# Revit family: E108.01.05_D9
name_source: partatom
category: Plumbing Fixtures
units: mm (PartAtom-declared; Revit-internal decimal feet)

## family parameters
Always vertical = Yes
Cut with Voids When Loaded = No
OmniClass Number = 23.45.05.14
OmniClass Title = Plumbing Fixtures - Sanitary Washing Units
Part Type = Normal
Room Calculation Point = No
Round Connector Dimension = Use Diameter
Shared = No
Work Plane-Based = No

## types (1)
- Standard
    Acabado = Cromo
    CW Connection = No
    Catalog web link = https://fvandina.com
    Certificación = INEN
    Conexión hidráulica = ½ x 14 NPT
    Cota alto = 150 mm
    Cota ancho = 120 mm
    Cota largo = 68 mm
    Default Elevation = 0 mm  [stored 0 ft]
    Description = Juego Mezclador Monocomando para Ducha COTY
    Dirección fabricante = KM 25, VÍA SANGOLQUÍ AMAGUAÑA - PICHINCHA - ECUADOR
    Garantía = GARANTÍA TOTAL FV - DETALLES EN PÁGINA WEB
    HW Connection = No
    Instalación = https://fvandina.com
    Manufacturer = FV - AREA ANDINA S.A.
    Material = Latón
    Model = E108.01.05/D9
    Part Number = E108.01.05/D9
    Presión = 60 PSI
    Title = Juego Mezclador Monocomando para Ducha COTY
    URL = www.fvandina.com
    Vent Connection = No
    Waste Connection = No

note: [stored X ft] marks values corroborated as IEEE doubles in the binary element streams (Revit-internal decimal feet)

## geometry (parser evidence)
native form markers: Sweep x3
no freeform markers — native parametric forms only
